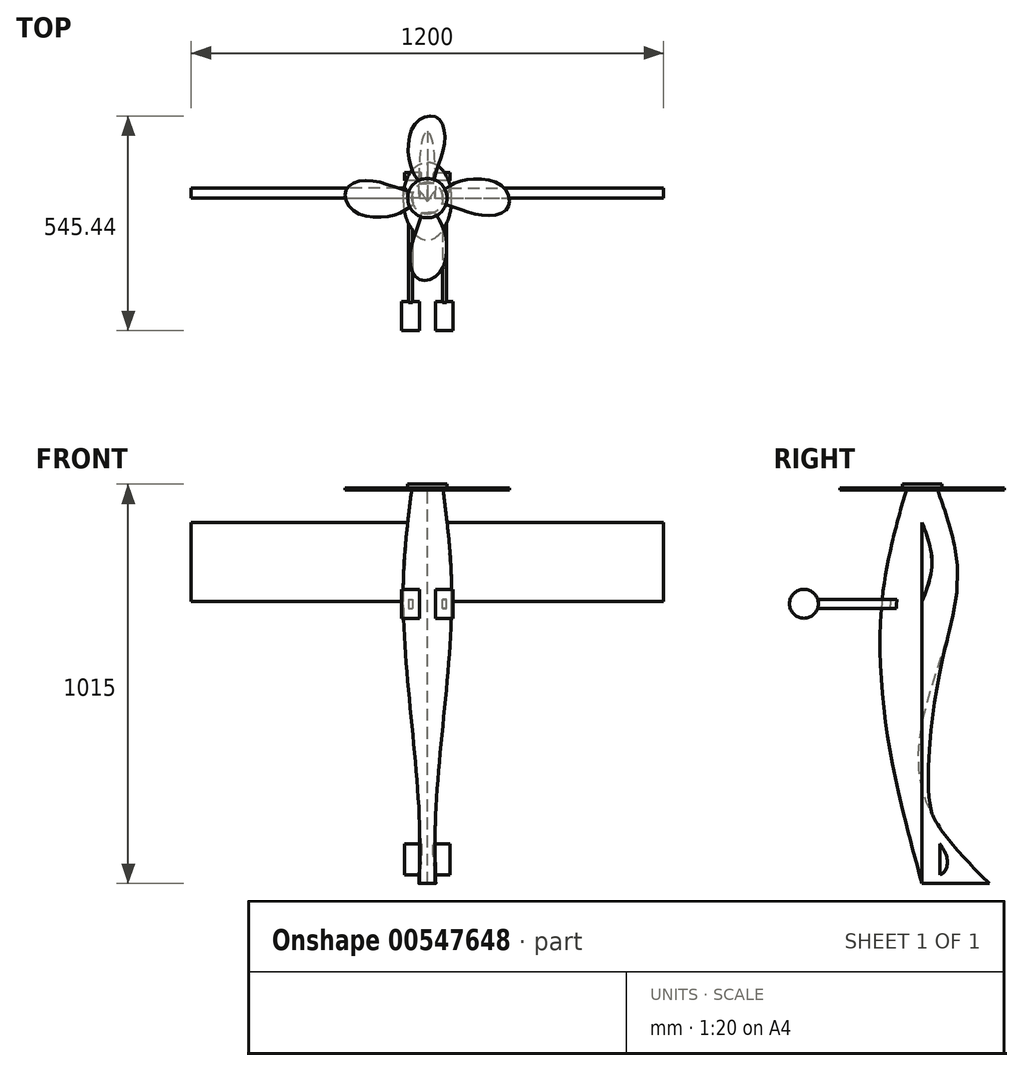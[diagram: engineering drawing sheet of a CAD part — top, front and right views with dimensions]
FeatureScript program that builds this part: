
annotation { "Feature Type Name" : "Feature", "Feature Type Description" : "" }
export const myFeature = defineFeature(function(context is Context, id is Id, definition is map)
    precondition{}
    {
        {
            var Q0;
            Q0=qCreatedBy(makeId("Top.planeOp"),FACE);
            cPlane(context, id + "F0", {"entities" : qUnion([Q0]), "cplaneType" : CPlaneType.OFFSET, "offset" : 1000 * mm, "width" : 150 * mm, "height" : 150 * mm});
        }
        {
            var Q0;
            Q0=qCreatedBy(makeId("Top.planeOp"),FACE);
            cPlane(context, id + "F1", {"entities" : qUnion([Q0]), "cplaneType" : CPlaneType.OFFSET, "offset" : 800 * mm, "width" : 150 * mm, "height" : 150 * mm});
        }
        {
            var Q0;
            Q0=qCreatedBy(makeId("Top.planeOp"),FACE);
            cPlane(context, id + "F2", {"entities" : qUnion([Q0]), "cplaneType" : CPlaneType.OFFSET, "offset" : 150 * mm, "width" : 150 * mm, "height" : 150 * mm});
        }
        {
            var Q0;
            Q0=qCreatedBy(makeId("Top.planeOp"),FACE);
            var sketch = newSketch(context, id + "F3", { "sketchPlane" : qUnion([Q0])});
            skLineSegment(sketch, "E0", {"start": v(-20, 0) * mm, "end": v(0, 0) * mm});
            skFitSpline(sketch, "E1", {"points": [v(-20, 0) * mm, v(-20.45, 60.33) * mm, v(0, 170.78) * mm], "startDerivative": vector(-15.16, 139.57) * mm, "endDerivative": vector(91.1, 58.9) * mm});
            skFitSpline(sketch, "E2.MirrorCS", {"points": [v(20, 0) * mm, v(20.45, 60.33) * mm, v(0, 170.78) * mm], "startDerivative": vector(15.16, 139.57) * mm, "endDerivative": vector(-91.1, 58.9) * mm});
            skLineSegment(sketch, "E3.MirrorCS", {"start": v(20, 0) * mm, "end": v(0, 0) * mm});
            skSolve(sketch);
        }
        {
            var Q0;
            Q0=qCreatedBy(id+"F2.planeOp",FACE);
            var sketch = newSketch(context, id + "F4", { "sketchPlane" : qUnion([Q0])});
            skEllipse(sketch, "E4", {"center": v(0, 0) * mm, "majorRadius": 40 * mm, "minorRadius": 20 * mm, "majorAxis": v(0, 1)});
            skSolve(sketch);
        }
        {
            var Q0;
            Q0=qCreatedBy(id+"F1.planeOp",FACE);
            var sketch = newSketch(context, id + "F5", { "sketchPlane" : qUnion([Q0])});
            skEllipse(sketch, "E5", {"center": v(0, 0) * mm, "majorRadius": 90 * mm, "minorRadius": 60 * mm, "majorAxis": v(0, 1)});
            skSolve(sketch);
        }
        {
            var Q0;
            Q0=qCreatedBy(id+"F0.planeOp",FACE);
            var sketch = newSketch(context, id + "F6", { "sketchPlane" : qUnion([Q0])});
            skEllipse(sketch, "E6", {"center": v(0, 0) * mm, "majorRadius": 40 * mm, "minorRadius": 40 * mm, "majorAxis": v(0, 1)});
            skSolve(sketch);
        }
        {
            var Q0;
            Q0=makeQuery(id+"F3.imprint","IMPRINT",FACE,{"disambiguationData":[TD([[makeQuery(id+"F3.imprint","IMPRINT",EDGE,{"derivedFrom":sQuery(id+"F3.wireOp",EDGE,"E0")}),1.0]])]});
            var Q1;
            Q1=makeQuery(id+"F4.imprint","IMPRINT",FACE,{"disambiguationData":[TD([[makeQuery(id+"F4.imprint","IMPRINT",EDGE,{"derivedFrom":sQuery(id+"F4.wireOp",EDGE,"E4")}),1.0]])]});
            var Q2;
            Q2=makeQuery(id+"F5.imprint","IMPRINT",FACE,{"disambiguationData":[TD([[makeQuery(id+"F5.imprint","IMPRINT",EDGE,{"derivedFrom":sQuery(id+"F5.wireOp",EDGE,"E5")}),1.0]])]});
            var Q3;
            Q3=makeQuery(id+"F6.imprint","IMPRINT",FACE,{"disambiguationData":[TD([[makeQuery(id+"F6.imprint","IMPRINT",EDGE,{"derivedFrom":sQuery(id+"F6.wireOp",EDGE,"E6")}),1.0]])]});
            loft(context, id + "F7", {"sheetProfilesArray" : [{ "sheetProfileEntities" : qUnion([Q0]) }, { "sheetProfileEntities" : qUnion([Q1]) }, { "sheetProfileEntities" : qUnion([Q2]) }, { "sheetProfileEntities" : qUnion([Q3]) }]});
        }
        {
            var Q0;
            Q0=qCreatedBy(makeId("Right.planeOp"),FACE);
            var sketch = newSketch(context, id + "F8", { "sketchPlane" : qUnion([Q0])});
            skLineSegment(sketch, "E7", {"start": v(0, 717.23) * mm, "end": v(0, 918) * mm});
            skPoint(sketch, "E8.1.internal.snap0", {"position": v(0, 817.61) * mm});
            skFitSpline(sketch, "E8", {"points": [v(0, 717.23) * mm, v(25.17, 817.61) * mm, v(0, 918) * mm], "startDerivative": vector(76.35, 178.38) * mm, "endDerivative": vector(-74.8, 198.18) * mm});
            skSolve(sketch);
        }
        {
            var Q0;
            Q0 = qSketchRegion(id + "F8", true);
            extrude(context, id + "F9", {"entities" : qUnion([Q0]), "operationType" : NewBodyOperationType.ADD, "endBound" : BoundingType.SYMMETRIC, "oppositeDirection" : true, "depth" : 1200 * mm, "offsetDistance" : 25 * mm});
        }
        {
            var Q0;
            Q0=qCreatedBy(id+"F0.planeOp",FACE);
            var sketch = newSketch(context, id + "F10", { "sketchPlane" : qUnion([Q0])});
            skEllipse(sketch, "E9", {"center": v(0, 0) * mm, "majorRadius": 50 * mm, "minorRadius": 50 * mm, "majorAxis": v(0, 1)});
            skSolve(sketch);
        }
        {
            var Q0;
            Q0 = qSketchRegion(id + "F10", true);
            extrude(context, id + "F11", {"entities" : qUnion([Q0]), "operationType" : NewBodyOperationType.ADD, "depth" : 15 * mm, "offsetDistance" : 25 * mm});
        }
        {
            var Q0;
            Q0=qCreatedBy(id+"F0.planeOp",FACE);
            var sketch = newSketch(context, id + "F12", { "sketchPlane" : qUnion([Q0])});
            skFitSpline(sketch, "E10", {"points": [v(-16.27, 35.64) * mm, v(-46.05, 95.82) * mm, v(-30.5, 189.96) * mm, v(23.02, 205.25) * mm, v(44.28, 144.4) * mm, v(14.32, 37.85) * mm], "startDerivative": vector(-217.87, 272.75) * mm, "endDerivative": vector(-110.66, -475.04) * mm});
            skLineSegment(sketch, "E11", {"start": v(-16.27, 35.64) * mm, "end": v(14.32, 37.85) * mm});
            skSolve(sketch);
        }
        {
            var Q0;
            Q0=qCreatedBy(makeId("Right.planeOp"),FACE);
            var sketch = newSketch(context, id + "F13", { "sketchPlane" : qUnion([Q0])});
            skLineSegment(sketch, "E12", {"start": v(0, 0) * mm, "end": v(0, 1251.79) * mm, "construction": true});
            skSolve(sketch);
        }
        {
            var Q0;
            Q0=makeQuery(id+"F12.imprint","IMPRINT",FACE,{"disambiguationData":[TD([[makeQuery(id+"F12.imprint","IMPRINT",EDGE,{"derivedFrom":sQuery(id+"F12.wireOp",EDGE,"E10")}),-1.0]])]});
            extrude(context, id + "F14", {"entities" : qUnion([Q0]), "depth" : 5 * mm, "offsetDistance" : 25 * mm});
        }
        {
            var Q0;
            Q0=makeQuery(id+"F14.opExtrude","SWEPT_BODY",BODY,{"disambiguationData":[OSD([sQuery(id+"F12.wireOp",EDGE,"E10"),sQuery(id+"F12.wireOp",EDGE,"E11")])]});
            var Q1;
            Q1=sQuery(id+"F13.wireOp",EDGE,"E12");
            circularPattern(context, id + "F15", {"entities" : qUnion([Q0]), "axis" : qUnion([Q1]), "angle" : 360 * degree, "instanceCount" : 4, "equalSpace" : true});
        }
        {
            var Q0;
            Q0=qCreatedBy(makeId("Right.planeOp"),FACE);
            var sketch = newSketch(context, id + "F16", { "sketchPlane" : qUnion([Q0])});
            skLineSegment(sketch, "E13", {"start": v(44.98, 101.21) * mm, "end": v(44.98, 22.5) * mm});
            skFitSpline(sketch, "E14", {"points": [v(44.98, 101.21) * mm, v(64.1, 61.85) * mm, v(57.35, 30.93) * mm, v(44.98, 22.5) * mm], "startDerivative": vector(62.9, -93.39) * mm, "endDerivative": vector(-55.23, -23.8) * mm});
            skSolve(sketch);
        }
        {
            var Q0;
            Q0 = qSketchRegion(id + "F16", true);
            extrude(context, id + "F17", {"entities" : qUnion([Q0]), "operationType" : NewBodyOperationType.ADD, "endBound" : BoundingType.SYMMETRIC, "depth" : 115 * mm, "offsetDistance" : 25 * mm});
        }
        {
            var Q0;
            Q0=qCreatedBy(makeId("Right.planeOp"),FACE);
            cPlane(context, id + "F18", {"entities" : qUnion([Q0]), "cplaneType" : CPlaneType.OFFSET, "offset" : 38 * mm, "width" : 150 * mm, "height" : 150 * mm});
        }
        {
            var Q0;
            Q0=qCreatedBy(id+"F18.planeOp",FACE);
            var sketch = newSketch(context, id + "F19", { "sketchPlane" : qUnion([Q0])});
            skLineSegment(sketch, "E15.bottom", {"start": v(-34.12, 722.44) * mm, "end": v(-299.9, 722.44) * mm});
            skLineSegment(sketch, "E15.top", {"start": v(-34.12, 699.39) * mm, "end": v(-299.9, 699.39) * mm});
            skLineSegment(sketch, "E15.left", {"start": v(-34.12, 722.44) * mm, "end": v(-34.12, 699.39) * mm});
            skLineSegment(sketch, "E15.right", {"start": v(-299.9, 722.44) * mm, "end": v(-299.9, 699.39) * mm});
            skSolve(sketch);
        }
        {
            var Q0;
            Q0=makeQuery(id+"F19.imprint","IMPRINT",FACE,{"disambiguationData":[TD([[makeQuery(id+"F19.imprint","IMPRINT",EDGE,{"derivedFrom":sQuery(id+"F19.wireOp",EDGE,"E15.bottom")}),1.0]])]});
            extrude(context, id + "F20", {"entities" : qUnion([Q0]), "depth" : 10 * mm, "offsetDistance" : 25 * mm});
        }
        {
            var Q0;
            Q0=makeQuery(id+"F20.opExtrude","CAP_FACE",FACE,{"disambiguationData":[OSD([sQuery(id+"F19.wireOp",EDGE,"E15.bottom"),sQuery(id+"F19.wireOp",EDGE,"E15.top"),sQuery(id+"F19.wireOp",EDGE,"E15.left"),sQuery(id+"F19.wireOp",EDGE,"E15.right")])],"isStart":false});
            var sketch = newSketch(context, id + "F21", { "sketchPlane" : qUnion([Q0])});
            skCircle(sketch, "E16", {"center": v(-299.9, 710.92) * mm, "radius": 36.67 * mm});
            skSolve(sketch);
        }
        {
            var Q0;
            {var subQ5=makeQuery(id+"F20.opExtrude","CAP_EDGE",EDGE,{"disambiguationData":[OSD([sQuery(id+"F19.wireOp",EDGE,"E15.right")])],"isStart":false});Q0=makeQuery(id+"F21.imprint","IMPRINT",FACE,{"disambiguationData":[TD([[makeQuery(id+"F21.imprint","IMPRINT",EDGE,{"derivedFrom":subQ5}),-1.0]])]});}
            var Q1;
            {var subQ5=makeQuery(id+"F20.opExtrude","CAP_EDGE",EDGE,{"disambiguationData":[OSD([sQuery(id+"F19.wireOp",EDGE,"E15.right")])],"isStart":false});Q1=makeQuery(id+"F21.imprint","IMPRINT",FACE,{"disambiguationData":[TD([[makeQuery(id+"F21.imprint","IMPRINT",EDGE,{"derivedFrom":subQ5}),1.0]])]});}
            extrude(context, id + "F22", {"entities" : qUnion([Q0, Q1]), "depth" : 17.5 * mm, "offsetDistance" : 25 * mm});
        }
        {
            var Q0;
            Q0=makeQuery(id+"F22.opExtrude","CAP_FACE",FACE,{"disambiguationData":[OSD([sQuery(id+"F21.wireOp",EDGE,"E16")])],"isStart":false});
            extrude(context, id + "F23", {"entities" : qUnion([Q0]), "operationType" : NewBodyOperationType.ADD, "oppositeDirection" : true, "depth" : 45 * mm, "offsetDistance" : 25 * mm});
        }
        {
            var Q0;
            Q0=makeQuery(id+"F20.opExtrude","SWEPT_BODY",BODY,{"disambiguationData":[OSD([sQuery(id+"F19.wireOp",EDGE,"E15.bottom"),sQuery(id+"F19.wireOp",EDGE,"E15.top"),sQuery(id+"F19.wireOp",EDGE,"E15.left"),sQuery(id+"F19.wireOp",EDGE,"E15.right")])]});
            var Q1;
            Q1=makeQuery(id+"F22.opExtrude","SWEPT_BODY",BODY,{"disambiguationData":[OSD([sQuery(id+"F21.wireOp",EDGE,"E16")])]});
            var Q2;
            Q2=qCreatedBy(makeId("Right.planeOp"),FACE);
            mirror(context, id + "F24", {"operationType" : NewBodyOperationType.ADD, "entities" : qUnion([Q0, Q1]), "mirrorPlane" : qUnion([Q2])});
        }
    });
